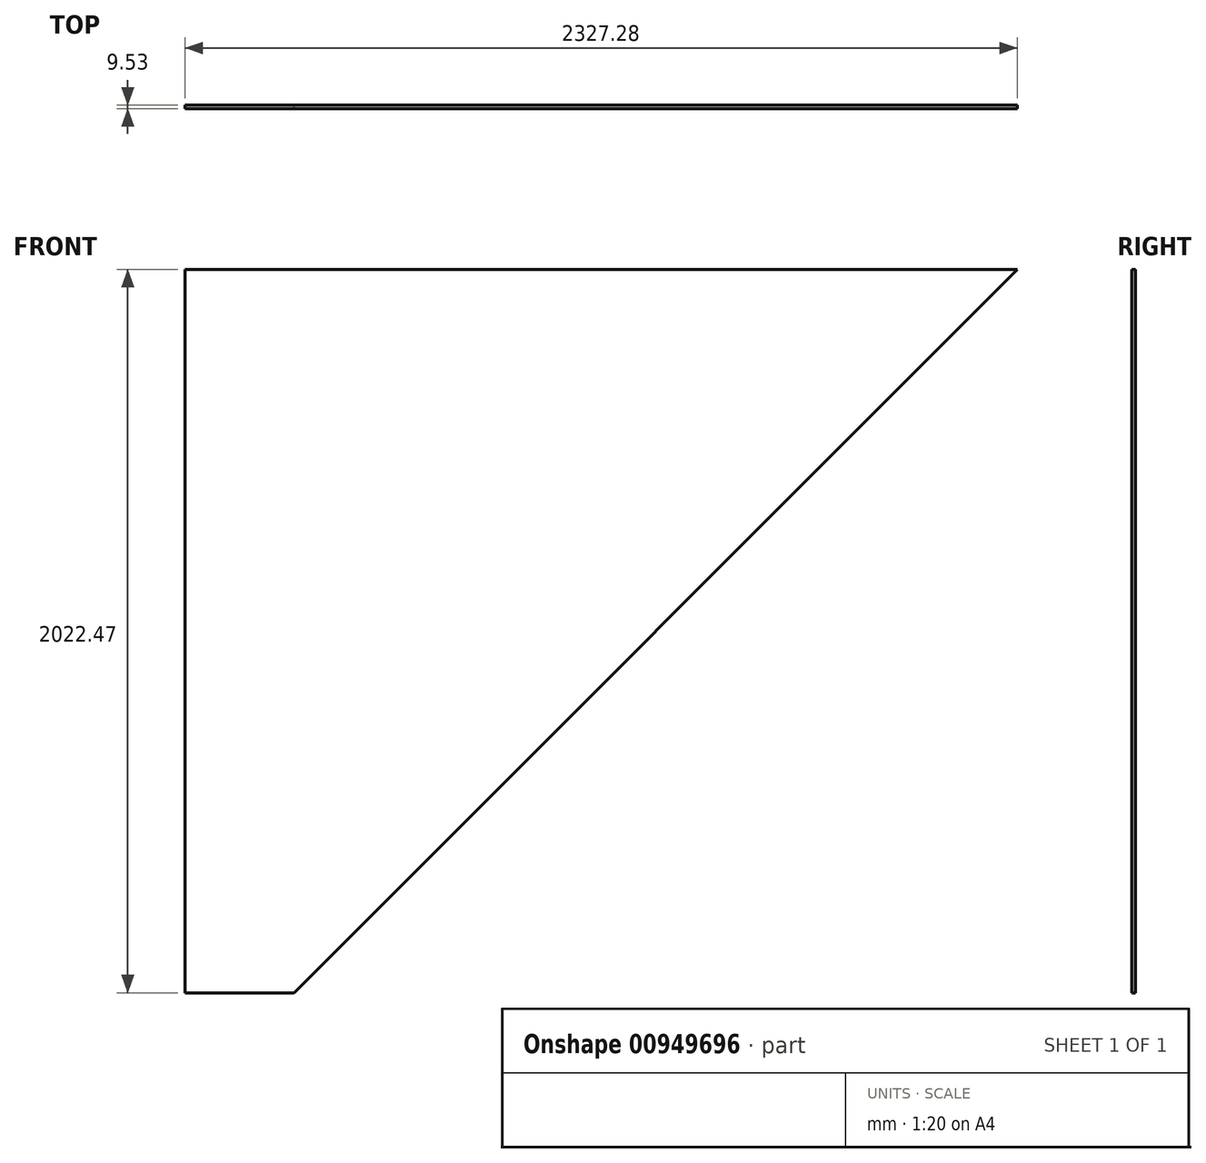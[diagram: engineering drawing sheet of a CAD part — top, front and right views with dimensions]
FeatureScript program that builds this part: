
annotation { "Feature Type Name" : "Feature", "Feature Type Description" : "" }
export const myFeature = defineFeature(function(context is Context, id is Id, definition is map)
    precondition{}
    {
        {
            var Q0;
            Q0=qCreatedBy(makeId("Front.planeOp"),FACE);
            var sketch = newSketch(context, id + "F0", { "sketchPlane" : qUnion([Q0])});
            skLineSegment(sketch, "E0", {"start": v(0, 0) * mm, "end": v(2327.28, 0) * mm});
            skLineSegment(sketch, "E1", {"start": v(2327.28, 0) * mm, "end": v(304.8, -2022.48) * mm});
            skLineSegment(sketch, "E2", {"start": v(304.8, -2022.48) * mm, "end": v(0, -2022.48) * mm});
            skLineSegment(sketch, "E3", {"start": v(0, -2022.48) * mm, "end": v(0, 0) * mm});
            skSolve(sketch);
        }
        {
            var Q0;
            Q0 = qSketchRegion(id + "F0", true);
            extrude(context, id + "F1", {"entities" : qUnion([Q0]), "depth" : 9.52 * mm, "offsetDistance" : 25.4 * mm});
        }
    });
